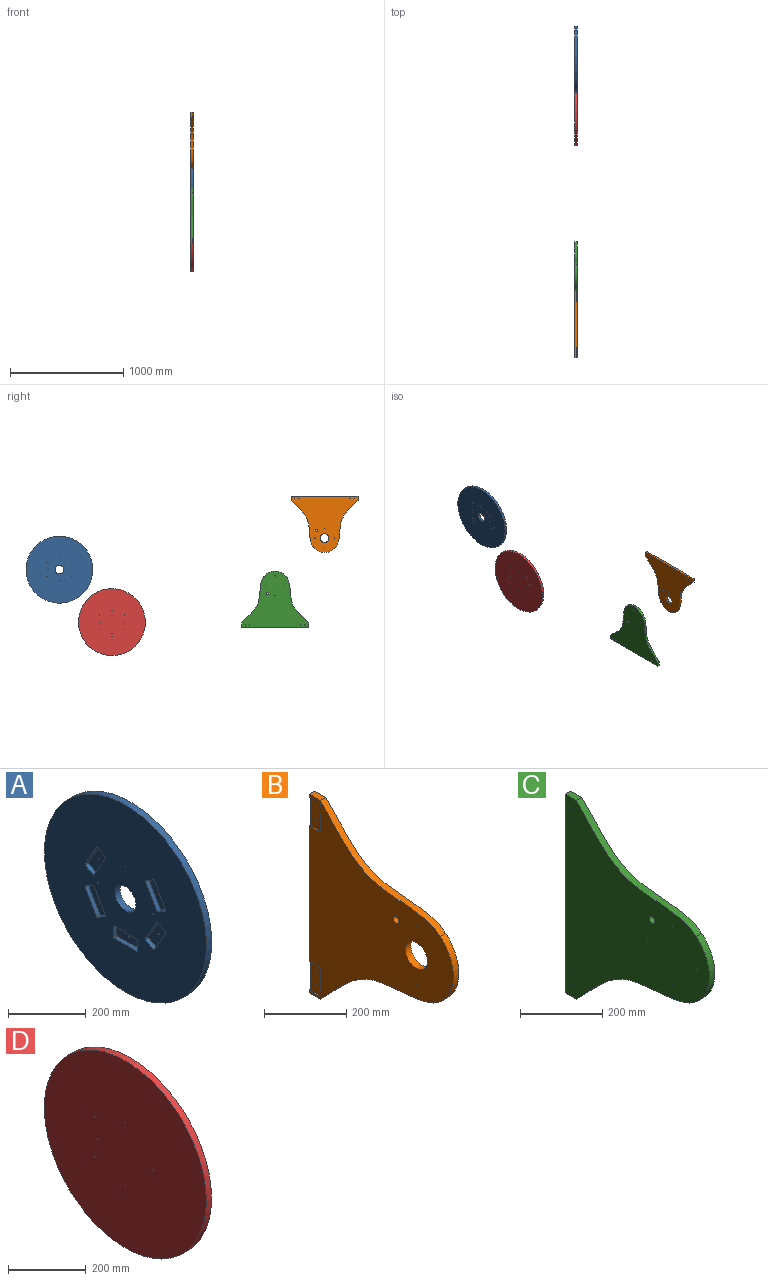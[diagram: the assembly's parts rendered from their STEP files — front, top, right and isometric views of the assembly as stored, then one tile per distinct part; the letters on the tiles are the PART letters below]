
ASSEMBLY  parts=4 mates=3
PART A: 58 faces, bbox 19.1x590.6x590.6 mm
  f0: plane 590.55x590.55mm, normal (-1,0,0), area 252436.7mm2, adj f1,f3,f4,f5,f6,f7,f8,f9
  f1: cylinder r=295.28mm len=590.55mm, axis (-1,0,0), area 35342.8mm2, adj f0,f2
  f2: plane 590.55x590.55mm, normal (1,0,0), area 269306.6mm2, adj f1,f48,f49,f50,f51,f52,f53,f54
  f3: cylinder r=3.17mm len=12.7mm, axis (1,0,0), area 63.3mm2, adj f0,f4,f10,f11
  f4: plane 71.49x41.28mm, normal (0,-0.87,0.5), area 1048.4mm2, adj f0,f3,f5,f11
  f5: cylinder r=3.17mm len=12.7mm, axis (1,0,0), area 63.3mm2, adj f0,f4,f6,f11
  f6: plane 27.5x15.88mm, normal (0,0.5,0.87), area 403.2mm2, adj f0,f5,f7,f11
  f7: cylinder r=3.17mm len=12.7mm, axis (1,0,0), area 63.3mm2, adj f0,f6,f8,f11
  f8: plane 71.49x41.28mm, normal (0,0.87,-0.5), area 1048.4mm2, adj f0,f7,f9,f11
  f9: cylinder r=3.17mm len=12.7mm, axis (1,0,0), area 63.3mm2, adj f0,f8,f10,f11
  f10: plane 27.5x15.88mm, normal (0,-0.5,-0.87), area 403.2mm2, adj f0,f3,f9,f11
  f11: plane 93.72x75.12mm, normal (-1,0,0), area 3374mm2, adj f3,f4,f5,f6,f7,f8,f9,f10
  f12: cylinder r=3.17mm len=12.7mm, axis (1,0,0), area 63.3mm2, adj f0,f13,f19,f20
  f13: plane 27.5x15.88mm, normal (0,0.5,0.87), area 403.2mm2, adj f0,f12,f14,f20
  f14: cylinder r=3.17mm len=12.7mm, axis (1,0,0), area 63.3mm2, adj f0,f13,f15,f20
  f15: plane 71.49x41.28mm, normal (0,0.87,-0.5), area 1048.4mm2, adj f0,f14,f16,f20
  f16: cylinder r=3.17mm len=12.7mm, axis (1,0,0), area 63.3mm2, adj f0,f15,f17,f20
  f17: plane 27.5x15.88mm, normal (0,-0.5,-0.87), area 403.2mm2, adj f0,f16,f18,f20
  f18: cylinder r=3.17mm len=12.7mm, axis (1,0,0), area 63.3mm2, adj f0,f17,f19,f20
  f19: plane 71.49x41.28mm, normal (0,-0.87,0.5), area 1048.4mm2, adj f0,f12,f18,f20
  f20: plane 93.72x75.12mm, normal (-1,0,0), area 3374mm2, adj f12,f13,f14,f15,f16,f17,f18,f19
  f21: cylinder r=3.17mm len=12.7mm, axis (1,0,0), area 63.3mm2, adj f0,f22,f28,f29
  f22: plane 71.49x41.28mm, normal (0,-0.87,-0.5), area 1048.4mm2, adj f0,f21,f23,f29
  f23: cylinder r=3.17mm len=12.7mm, axis (1,0,0), area 63.3mm2, adj f0,f22,f24,f29
  f24: plane 27.5x15.88mm, normal (0,-0.5,0.87), area 403.2mm2, adj f0,f23,f25,f29
  f25: cylinder r=3.17mm len=12.7mm, axis (1,0,0), area 63.3mm2, adj f0,f24,f26,f29
  f26: plane 71.49x41.28mm, normal (0,0.87,0.5), area 1048.4mm2, adj f0,f25,f27,f29
  f27: cylinder r=3.17mm len=12.7mm, axis (1,0,0), area 63.3mm2, adj f0,f26,f28,f29
  f28: plane 27.5x15.88mm, normal (0,0.5,-0.87), area 403.2mm2, adj f0,f21,f27,f29
  f29: plane 93.72x75.12mm, normal (-1,0,0), area 3374mm2, adj f21,f22,f23,f24,f25,f26,f27,f28
  f30: cylinder r=3.17mm len=12.7mm, axis (1,0,0), area 63.3mm2, adj f0,f31,f37,f38
  f31: plane 82.55x12.7mm, normal (0,0,-1), area 1048.4mm2, adj f0,f30,f32,f38
  f32: cylinder r=3.17mm len=12.7mm, axis (1,0,0), area 63.3mm2, adj f0,f31,f33,f38
  f33: plane 31.75x12.7mm, normal (0,-1,0), area 403.2mm2, adj f0,f32,f34,f38
  f34: cylinder r=3.17mm len=12.7mm, axis (1,0,0), area 63.3mm2, adj f0,f33,f35,f38
  f35: plane 82.55x12.7mm, normal (0,0,1), area 1048.4mm2, adj f0,f34,f36,f38
  f36: cylinder r=3.17mm len=12.7mm, axis (1,0,0), area 63.3mm2, adj f0,f35,f37,f38
  f37: plane 31.75x12.7mm, normal (0,1,0), area 403.2mm2, adj f0,f30,f36,f38
  f38: plane 88.9x38.1mm, normal (-1,0,0), area 3374mm2, adj f30,f31,f32,f33,f34,f35,f36,f37
  f39: cylinder r=3.17mm len=12.7mm, axis (1,0,0), area 63.3mm2, adj f0,f40,f46,f47
  f40: plane 27.5x15.88mm, normal (0,-0.5,0.87), area 403.2mm2, adj f0,f39,f41,f47
  f41: cylinder r=3.17mm len=12.7mm, axis (1,0,0), area 63.3mm2, adj f0,f40,f42,f47
  f42: plane 71.49x41.28mm, normal (0,0.87,0.5), area 1048.4mm2, adj f0,f41,f43,f47
  f43: cylinder r=3.17mm len=12.7mm, axis (1,0,0), area 63.3mm2, adj f0,f42,f44,f47
  f44: plane 27.5x15.88mm, normal (0,0.5,-0.87), area 403.2mm2, adj f0,f43,f45,f47
  f45: cylinder r=3.17mm len=12.7mm, axis (1,0,0), area 63.3mm2, adj f0,f44,f46,f47
  f46: plane 71.49x41.28mm, normal (0,-0.87,-0.5), area 1048.4mm2, adj f0,f39,f45,f47
  f47: plane 93.72x75.12mm, normal (-1,0,0), area 3374mm2, adj f39,f40,f41,f42,f43,f44,f45,f46
  f48: cylinder r=38.1mm len=76.2mm, axis (1,0,0), area 4560.4mm2, adj f0,f2
  f49: cylinder r=1.19mm len=6.35mm, axis (-1,0,0), area 47.5mm2, adj f2,f47
  f50: cylinder r=1.19mm len=6.35mm, axis (-1,0,0), area 47.5mm2, adj f2,f38
  f51: cylinder r=1.19mm len=6.35mm, axis (-1,0,0), area 47.5mm2, adj f2,f29
  f52: cylinder r=1.19mm len=6.35mm, axis (-1,0,0), area 47.5mm2, adj f2,f20
  f53: cylinder r=1.19mm len=6.35mm, axis (-1,0,0), area 47.5mm2, adj f2,f11
  f54: cylinder r=1.19mm len=19.05mm, axis (-1,0,0), area 142.5mm2, adj f0,f2
  f55: cylinder r=1.19mm len=19.05mm, axis (-1,0,0), area 142.5mm2, adj f0,f2
  f56: cylinder r=1.19mm len=19.05mm, axis (-1,0,0), area 142.5mm2, adj f0,f2
  f57: cylinder r=1.19mm len=19.05mm, axis (-1,0,0), area 142.5mm2, adj f0,f2
PART B: 34 faces, bbox 19.1x495.3x590.6 mm
  f0: plane 590.55x495.3mm, normal (1,0,0), area 159565.4mm2, adj f1,f3,f4,f5,f6,f7,f8,f25
  f1: plane 590.55x19.05mm, normal (0,1,0), area 10495.1mm2, adj f0,f2,f3,f4,f9,f10,f16,f17
  f2: plane 590.55x495.3mm, normal (-1,0,0), area 152921.1mm2, adj f1,f3,f4,f5,f6,f7,f8,f9
  f3: plane 38.1x19.05mm, normal (0,0,-1), area 725.8mm2, adj f0,f1,f2,f7
  f4: plane 38.1x19.05mm, normal (0,0,1), area 725.8mm2, adj f0,f1,f2,f5
  f5: extruded ~411.79x197.95mm, area 9052.9mm2, adj f0,f2,f4,f6
  f6: cylinder r=127mm len=194.64mm, axis (-1,0,0), area 4224.5mm2, adj f0,f2,f5,f7
  f7: extruded ~411.79x197.95mm, area 9052.9mm2, adj f0,f2,f3,f6
  f8: cylinder r=38.1mm len=76.2mm, axis (1,0,0), area 4560.4mm2, adj f0,f2
  f9: cylinder r=3.17mm len=4.57mm, axis (1,0,0), area 22.8mm2, adj f1,f2,f15,f16
  f10: cylinder r=3.17mm len=4.57mm, axis (1,0,0), area 22.8mm2, adj f1,f2,f11,f16
  f11: plane 31.22x4.57mm, normal (0,0,1), area 142.7mm2, adj f2,f10,f12,f16
  f12: cylinder r=3.17mm len=4.57mm, axis (1,0,0), area 22.8mm2, adj f2,f11,f13,f16
  f13: plane 82.55x4.57mm, normal (0,1,0), area 377.4mm2, adj f2,f12,f14,f16
  f14: cylinder r=3.17mm len=4.57mm, axis (1,0,0), area 22.8mm2, adj f2,f13,f15,f16
  f15: plane 31.22x4.57mm, normal (0,0,-1), area 142.7mm2, adj f2,f9,f14,f16
  f16: plane 88.9x37.57mm, normal (-1,0,0), area 3322.2mm2, adj f1,f9,f10,f11,f12,f13,f14,f15
  f17: cylinder r=3.17mm len=4.57mm, axis (1,0,0), area 22.8mm2, adj f1,f2,f18,f24
  f18: plane 31.22x4.57mm, normal (0,0,1), area 142.7mm2, adj f2,f17,f19,f24
  f19: cylinder r=3.17mm len=4.57mm, axis (1,0,0), area 22.8mm2, adj f2,f18,f20,f24
  f20: plane 82.55x4.57mm, normal (0,1,0), area 377.4mm2, adj f2,f19,f21,f24
  f21: cylinder r=3.17mm len=4.57mm, axis (1,0,0), area 22.8mm2, adj f2,f20,f22,f24
  f22: plane 31.22x4.57mm, normal (0,0,-1), area 142.7mm2, adj f2,f21,f23,f24
  f23: cylinder r=3.17mm len=4.57mm, axis (1,0,0), area 22.8mm2, adj f1,f2,f22,f24
  f24: plane 88.9x37.57mm, normal (-1,0,0), area 3322.2mm2, adj f1,f17,f18,f19,f20,f21,f22,f23
  f25: cylinder r=1.19mm len=14.48mm, axis (1,0,0), area 108.3mm2, adj f0,f24
  f26: cylinder r=1.19mm len=14.48mm, axis (1,0,0), area 108.3mm2, adj f0,f24
  f27: cylinder r=1.19mm len=14.48mm, axis (1,0,0), area 108.3mm2, adj f0,f16
  f28: cylinder r=1.19mm len=14.48mm, axis (1,0,0), area 108.3mm2, adj f0,f16
  f29: cylinder r=1.19mm len=19.05mm, axis (1,0,0), area 142.5mm2, adj f0,f2
  f30: cylinder r=9.53mm len=19.05mm, axis (1,0,0), area 1140.1mm2, adj f0,f2
  f31: cylinder r=1.19mm len=19.05mm, axis (1,0,0), area 142.5mm2, adj f0,f2
  f32: cylinder r=1.19mm len=19.05mm, axis (1,0,0), area 142.5mm2, adj f0,f2
  f33: cylinder r=1.19mm len=19.05mm, axis (1,0,0), area 142.5mm2, adj f0,f2
PART C: 33 faces, bbox 19.1x495.3x590.6 mm
  f0: plane 590.55x495.3mm, normal (-1,0,0), area 164125.8mm2, adj f1,f3,f4,f5,f6,f7,f24,f25
  f1: plane 590.55x19.05mm, normal (0,1,0), area 10495.1mm2, adj f0,f2,f3,f4,f8,f9,f15,f16
  f2: plane 590.55x495.3mm, normal (1,0,0), area 157481.5mm2, adj f1,f3,f4,f5,f6,f7,f8,f9
  f3: plane 38.1x19.05mm, normal (0,0,-1), area 725.8mm2, adj f0,f1,f2,f7
  f4: plane 38.1x19.05mm, normal (0,0,1), area 725.8mm2, adj f0,f1,f2,f5
  f5: extruded ~411.79x197.95mm, area 9052.9mm2, adj f0,f2,f4,f6
  f6: cylinder r=127mm len=194.64mm, axis (1,0,0), area 4224.5mm2, adj f0,f2,f5,f7
  f7: extruded ~411.79x197.95mm, area 9052.9mm2, adj f0,f2,f3,f6
  f8: cylinder r=3.17mm len=4.57mm, axis (1,0,0), area 22.8mm2, adj f1,f2,f14,f15
  f9: cylinder r=3.17mm len=4.57mm, axis (1,0,0), area 22.8mm2, adj f1,f2,f10,f15
  f10: plane 31.22x4.57mm, normal (0,0,1), area 142.7mm2, adj f2,f9,f11,f15
  f11: cylinder r=3.17mm len=4.57mm, axis (1,0,0), area 22.8mm2, adj f2,f10,f12,f15
  f12: plane 82.55x4.57mm, normal (0,1,0), area 377.4mm2, adj f2,f11,f13,f15
  f13: cylinder r=3.17mm len=4.57mm, axis (1,0,0), area 22.8mm2, adj f2,f12,f14,f15
  f14: plane 31.22x4.57mm, normal (0,0,-1), area 142.7mm2, adj f2,f8,f13,f15
  f15: plane 88.9x37.57mm, normal (1,0,0), area 3322.2mm2, adj f1,f8,f9,f10,f11,f12,f13,f14
  f16: cylinder r=3.17mm len=4.57mm, axis (1,0,0), area 22.8mm2, adj f1,f2,f17,f23
  f17: plane 31.22x4.57mm, normal (0,0,1), area 142.7mm2, adj f2,f16,f18,f23
  f18: cylinder r=3.17mm len=4.57mm, axis (1,0,0), area 22.8mm2, adj f2,f17,f19,f23
  f19: plane 82.55x4.57mm, normal (0,1,0), area 377.4mm2, adj f2,f18,f20,f23
  f20: cylinder r=3.17mm len=4.57mm, axis (1,0,0), area 22.8mm2, adj f2,f19,f21,f23
  f21: plane 31.22x4.57mm, normal (0,0,-1), area 142.7mm2, adj f2,f20,f22,f23
  f22: cylinder r=3.17mm len=4.57mm, axis (1,0,0), area 22.8mm2, adj f1,f2,f21,f23
  f23: plane 88.9x37.57mm, normal (1,0,0), area 3322.2mm2, adj f1,f16,f17,f18,f19,f20,f21,f22
  f24: cylinder r=1.19mm len=14.48mm, axis (1,0,0), area 108.3mm2, adj f0,f23
  f25: cylinder r=1.19mm len=14.48mm, axis (1,0,0), area 108.3mm2, adj f0,f23
  f26: cylinder r=1.19mm len=14.48mm, axis (1,0,0), area 108.3mm2, adj f0,f15
  f27: cylinder r=1.19mm len=14.48mm, axis (1,0,0), area 108.3mm2, adj f0,f15
  f28: cylinder r=1.19mm len=19.05mm, axis (1,0,0), area 142.5mm2, adj f0,f2
  f29: cylinder r=9.53mm len=19.05mm, axis (1,0,0), area 1140.1mm2, adj f0,f2
  f30: cylinder r=1.19mm len=19.05mm, axis (1,0,0), area 142.5mm2, adj f0,f2
  f31: cylinder r=1.19mm len=19.05mm, axis (1,0,0), area 142.5mm2, adj f0,f2
  f32: cylinder r=1.19mm len=19.05mm, axis (1,0,0), area 142.5mm2, adj f0,f2
PART D: 57 faces, bbox 19.1x590.6x590.6 mm
  f0: plane 590.55x590.55mm, normal (1,0,0), area 256997.1mm2, adj f1,f3,f4,f5,f6,f7,f8,f9
  f1: cylinder r=295.28mm len=590.55mm, axis (1,0,0), area 35342.8mm2, adj f0,f2
  f2: plane 590.55x590.55mm, normal (-1,0,0), area 273867mm2, adj f1,f48,f49,f50,f51,f52,f53,f54
  f3: cylinder r=3.17mm len=12.7mm, axis (1,0,0), area 63.3mm2, adj f0,f4,f10,f11
  f4: plane 71.49x41.28mm, normal (0,-0.87,0.5), area 1048.4mm2, adj f0,f3,f5,f11
  f5: cylinder r=3.17mm len=12.7mm, axis (1,0,0), area 63.3mm2, adj f0,f4,f6,f11
  f6: plane 27.5x15.88mm, normal (0,0.5,0.87), area 403.2mm2, adj f0,f5,f7,f11
  f7: cylinder r=3.17mm len=12.7mm, axis (1,0,0), area 63.3mm2, adj f0,f6,f8,f11
  f8: plane 71.49x41.28mm, normal (0,0.87,-0.5), area 1048.4mm2, adj f0,f7,f9,f11
  f9: cylinder r=3.17mm len=12.7mm, axis (1,0,0), area 63.3mm2, adj f0,f8,f10,f11
  f10: plane 27.5x15.88mm, normal (0,-0.5,-0.87), area 403.2mm2, adj f0,f3,f9,f11
  f11: plane 93.72x75.12mm, normal (1,0,0), area 3374mm2, adj f3,f4,f5,f6,f7,f8,f9,f10
  f12: cylinder r=3.17mm len=12.7mm, axis (1,0,0), area 63.3mm2, adj f0,f13,f19,f20
  f13: plane 27.5x15.88mm, normal (0,0.5,0.87), area 403.2mm2, adj f0,f12,f14,f20
  f14: cylinder r=3.17mm len=12.7mm, axis (1,0,0), area 63.3mm2, adj f0,f13,f15,f20
  f15: plane 71.49x41.28mm, normal (0,0.87,-0.5), area 1048.4mm2, adj f0,f14,f16,f20
  f16: cylinder r=3.17mm len=12.7mm, axis (1,0,0), area 63.3mm2, adj f0,f15,f17,f20
  f17: plane 27.5x15.88mm, normal (0,-0.5,-0.87), area 403.2mm2, adj f0,f16,f18,f20
  f18: cylinder r=3.17mm len=12.7mm, axis (1,0,0), area 63.3mm2, adj f0,f17,f19,f20
  f19: plane 71.49x41.28mm, normal (0,-0.87,0.5), area 1048.4mm2, adj f0,f12,f18,f20
  f20: plane 93.72x75.12mm, normal (1,0,0), area 3374mm2, adj f12,f13,f14,f15,f16,f17,f18,f19
  f21: cylinder r=3.17mm len=12.7mm, axis (1,0,0), area 63.3mm2, adj f0,f22,f28,f29
  f22: plane 71.49x41.28mm, normal (0,-0.87,-0.5), area 1048.4mm2, adj f0,f21,f23,f29
  f23: cylinder r=3.17mm len=12.7mm, axis (1,0,0), area 63.3mm2, adj f0,f22,f24,f29
  f24: plane 27.5x15.88mm, normal (0,-0.5,0.87), area 403.2mm2, adj f0,f23,f25,f29
  f25: cylinder r=3.17mm len=12.7mm, axis (1,0,0), area 63.3mm2, adj f0,f24,f26,f29
  f26: plane 71.49x41.28mm, normal (0,0.87,0.5), area 1048.4mm2, adj f0,f25,f27,f29
  f27: cylinder r=3.17mm len=12.7mm, axis (1,0,0), area 63.3mm2, adj f0,f26,f28,f29
  f28: plane 27.5x15.88mm, normal (0,0.5,-0.87), area 403.2mm2, adj f0,f21,f27,f29
  f29: plane 93.72x75.12mm, normal (1,0,0), area 3374mm2, adj f21,f22,f23,f24,f25,f26,f27,f28
  f30: cylinder r=3.17mm len=12.7mm, axis (1,0,0), area 63.3mm2, adj f0,f31,f37,f38
  f31: plane 82.55x12.7mm, normal (0,0,-1), area 1048.4mm2, adj f0,f30,f32,f38
  f32: cylinder r=3.17mm len=12.7mm, axis (1,0,0), area 63.3mm2, adj f0,f31,f33,f38
  f33: plane 31.75x12.7mm, normal (0,-1,0), area 403.2mm2, adj f0,f32,f34,f38
  f34: cylinder r=3.17mm len=12.7mm, axis (1,0,0), area 63.3mm2, adj f0,f33,f35,f38
  f35: plane 82.55x12.7mm, normal (0,0,1), area 1048.4mm2, adj f0,f34,f36,f38
  f36: cylinder r=3.17mm len=12.7mm, axis (1,0,0), area 63.3mm2, adj f0,f35,f37,f38
  f37: plane 31.75x12.7mm, normal (0,1,0), area 403.2mm2, adj f0,f30,f36,f38
  f38: plane 88.9x38.1mm, normal (1,0,0), area 3374mm2, adj f30,f31,f32,f33,f34,f35,f36,f37
  f39: cylinder r=3.17mm len=12.7mm, axis (1,0,0), area 63.3mm2, adj f0,f40,f46,f47
  f40: plane 27.5x15.88mm, normal (0,-0.5,0.87), area 403.2mm2, adj f0,f39,f41,f47
  f41: cylinder r=3.17mm len=12.7mm, axis (1,0,0), area 63.3mm2, adj f0,f40,f42,f47
  f42: plane 71.49x41.28mm, normal (0,0.87,0.5), area 1048.4mm2, adj f0,f41,f43,f47
  f43: cylinder r=3.17mm len=12.7mm, axis (1,0,0), area 63.3mm2, adj f0,f42,f44,f47
  f44: plane 27.5x15.88mm, normal (0,0.5,-0.87), area 403.2mm2, adj f0,f43,f45,f47
  f45: cylinder r=3.17mm len=12.7mm, axis (1,0,0), area 63.3mm2, adj f0,f44,f46,f47
  f46: plane 71.49x41.28mm, normal (0,-0.87,-0.5), area 1048.4mm2, adj f0,f39,f45,f47
  f47: plane 93.72x75.12mm, normal (1,0,0), area 3374mm2, adj f39,f40,f41,f42,f43,f44,f45,f46
  f48: cylinder r=1.19mm len=6.35mm, axis (1,0,0), area 47.5mm2, adj f2,f47
  f49: cylinder r=1.19mm len=6.35mm, axis (1,0,0), area 47.5mm2, adj f2,f38
  f50: cylinder r=1.19mm len=6.35mm, axis (1,0,0), area 47.5mm2, adj f2,f29
  f51: cylinder r=1.19mm len=6.35mm, axis (1,0,0), area 47.5mm2, adj f2,f20
  f52: cylinder r=1.19mm len=6.35mm, axis (1,0,0), area 47.5mm2, adj f2,f11
  f53: cylinder r=1.19mm len=19.05mm, axis (1,0,0), area 142.5mm2, adj f0,f2
  f54: cylinder r=1.19mm len=19.05mm, axis (1,0,0), area 142.5mm2, adj f0,f2
  f55: cylinder r=1.19mm len=19.05mm, axis (1,0,0), area 142.5mm2, adj f0,f2
  f56: cylinder r=1.19mm len=19.05mm, axis (1,0,0), area 142.5mm2, adj f0,f2
PLACE A rot(axis=(0,1,0),180deg) t=(-1784.43,207.29,272.66)mm
PLACE B rot(axis=(0,-0.71,-0.71),180deg) t=(-1757.26,-2134.6,551.38)mm
PLACE C rot(axis=(-1,0,0),90deg) t=(-1430.23,-1697.78,132.2)mm
PLACE D t=(-1457.41,-256.34,-190.74)mm
MATE planar B.f0 <-> A.f1  axis (-1,0,0) through (-1803.48,-2134.73,730.72)mm
MATE planar C.f0 <-> D.f1  axis (-1,0,0) through (-1803.48,-1697.91,-42.16)mm
MATE planar A.f1 <-> D.f1  axis (-1,0,0) through (-1803.48,207.29,272.65)mm
